# Revit family: Folding_Shower_Seat-Bobrick-B-51815
name_source: partatom
category: Specialty Equipment
units: mm (PartAtom-declared; Revit-internal decimal feet)

## family parameters
Cut with Voids When Loaded = No
Host = Face
OmniClass Number = 23.40.20.21
OmniClass Title = Toilet and Bath Specialties
Part Type = Normal
Room Calculation Point = No
Round Connector Dimension = Use Diameter
Shared = No

## types (1)
- B-51815
    ADA Compliant = Yes
    Assembly Code = C1030200
    Default Elevation = 19"
    Description = Reversible Seat With Swing Down Leg Shower Seat
    Finish = Metal-Bobrick-Stainless Steel
    Finish - Seat = Phenolic-Bobrick-White
    Height = 17"
    Installation Type = Wall Mounted
    Length = 33"
    Manufacturer = Bobrick
    Material = Metal-Bobrick-Stainless Steel
    Model = B-51815
    Mounting Height = 17"
    Mounting Height Constraint = 17"
    URL = https://www.bobrick.com
    Width = 20 15/16"

## geometry (parser evidence)
native form markers: Sweep x3
no freeform markers — native parametric forms only
